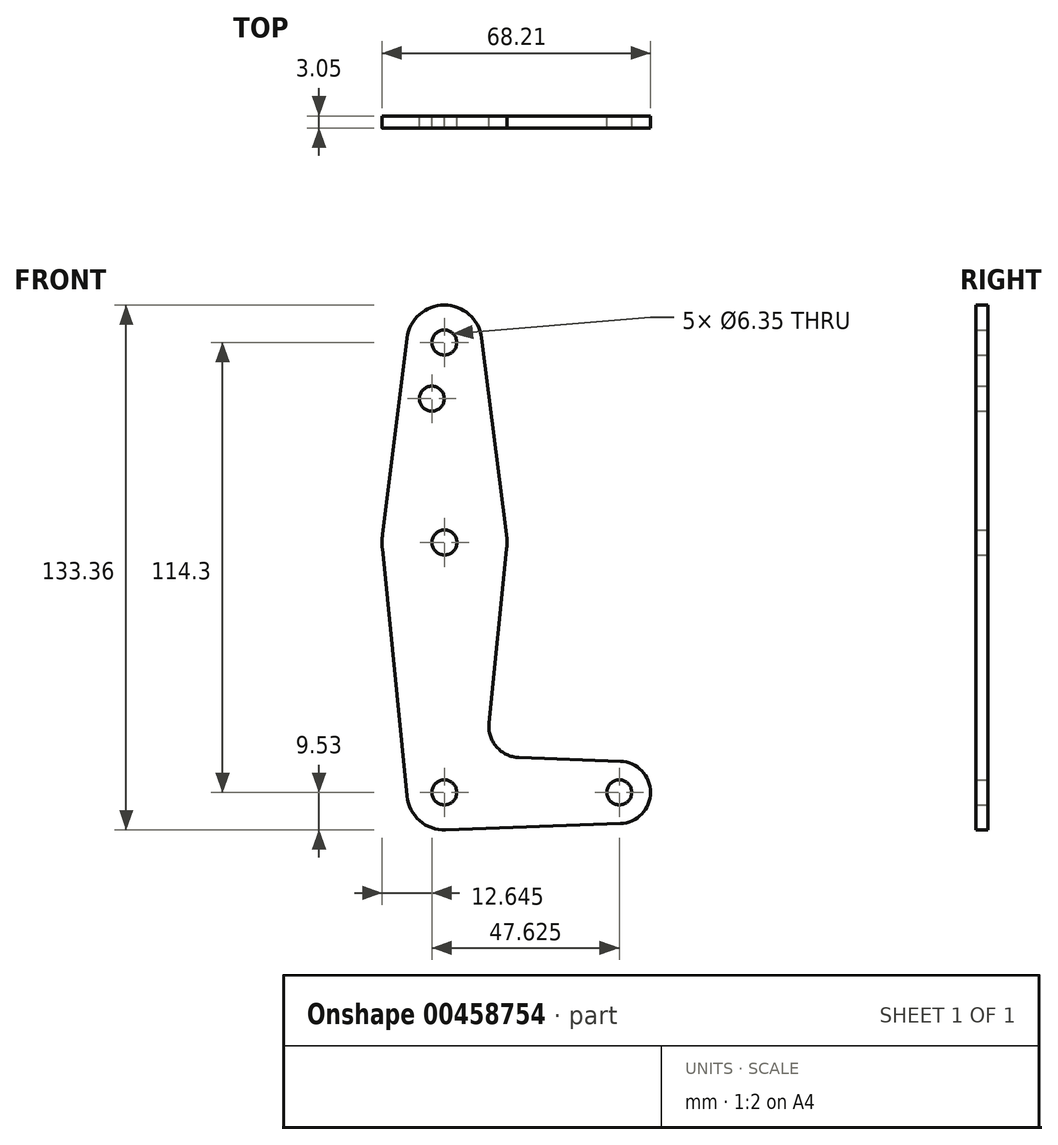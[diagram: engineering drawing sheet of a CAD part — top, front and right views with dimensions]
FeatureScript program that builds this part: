
annotation { "Feature Type Name" : "Feature", "Feature Type Description" : "" }
export const myFeature = defineFeature(function(context is Context, id is Id, definition is map)
    precondition{}
    {
        {
            var Q0;
            Q0=qCreatedBy(makeId("Front.planeOp"),FACE);
            var sketch = newSketch(context, id + "F0", { "sketchPlane" : qUnion([Q0])});
            skCircle(sketch, "E0", {"center": v(0, 114.3) * mm, "radius": 9.53 * mm});
            skCircle(sketch, "E1", {"center": v(0.05, 63.5) * mm, "radius": 15.88 * mm});
            skCircle(sketch, "E2", {"center": v(0, 0) * mm, "radius": 9.53 * mm});
            skCircle(sketch, "E3", {"center": v(44.45, 0) * mm, "radius": 7.94 * mm});
            skLineSegment(sketch, "E4", {"start": v(0, 114.3) * mm, "end": v(0, 0) * mm, "construction": true});
            skLineSegment(sketch, "E5", {"start": v(0, 0) * mm, "end": v(44.45, 0) * mm, "construction": true});
            skLineSegment(sketch, "E6", {"start": v(18.98, 8.85) * mm, "end": v(44.73, 7.93) * mm});
            skLineSegment(sketch, "E7", {"start": v(-9.48, -0.94) * mm, "end": v(-15.75, 61.93) * mm});
            skLineSegment(sketch, "E8", {"start": v(0.34, -9.52) * mm, "end": v(44.73, -7.93) * mm});
            skLineSegment(sketch, "E9", {"start": v(15.85, 61.9) * mm, "end": v(11.36, 17.6) * mm});
            skLineSegment(sketch, "E10", {"start": v(-9.45, 115.48) * mm, "end": v(-15.7, 65.47) * mm});
            skLineSegment(sketch, "E11", {"start": v(9.45, 115.5) * mm, "end": v(15.8, 65.5) * mm});
            skCircle(sketch, "E12", {"center": v(0, 114.3) * mm, "radius": 3.18 * mm});
            skCircle(sketch, "E13", {"center": v(-3.17, 100.04) * mm, "radius": 3.18 * mm});
            skCircle(sketch, "E14", {"center": v(0.05, 63.5) * mm, "radius": 3.18 * mm});
            skCircle(sketch, "E15", {"center": v(0, 0) * mm, "radius": 3.18 * mm});
            skCircle(sketch, "E16", {"center": v(44.45, 0) * mm, "radius": 3.18 * mm});
            skArc(sketch, "E17.filletArc", {"start": v(11.36, 17.6) * mm, "mid": v(13.27, 11.57) * mm, "end": v(18.98, 8.85) * mm});
            skSolve(sketch);
        }
        {
            var Q0;
            Q0 = qSketchRegion(id + "F0", true);
            extrude(context, id + "F1", {"entities" : qUnion([Q0]), "depth" : 3.05 * mm});
        }
    });
